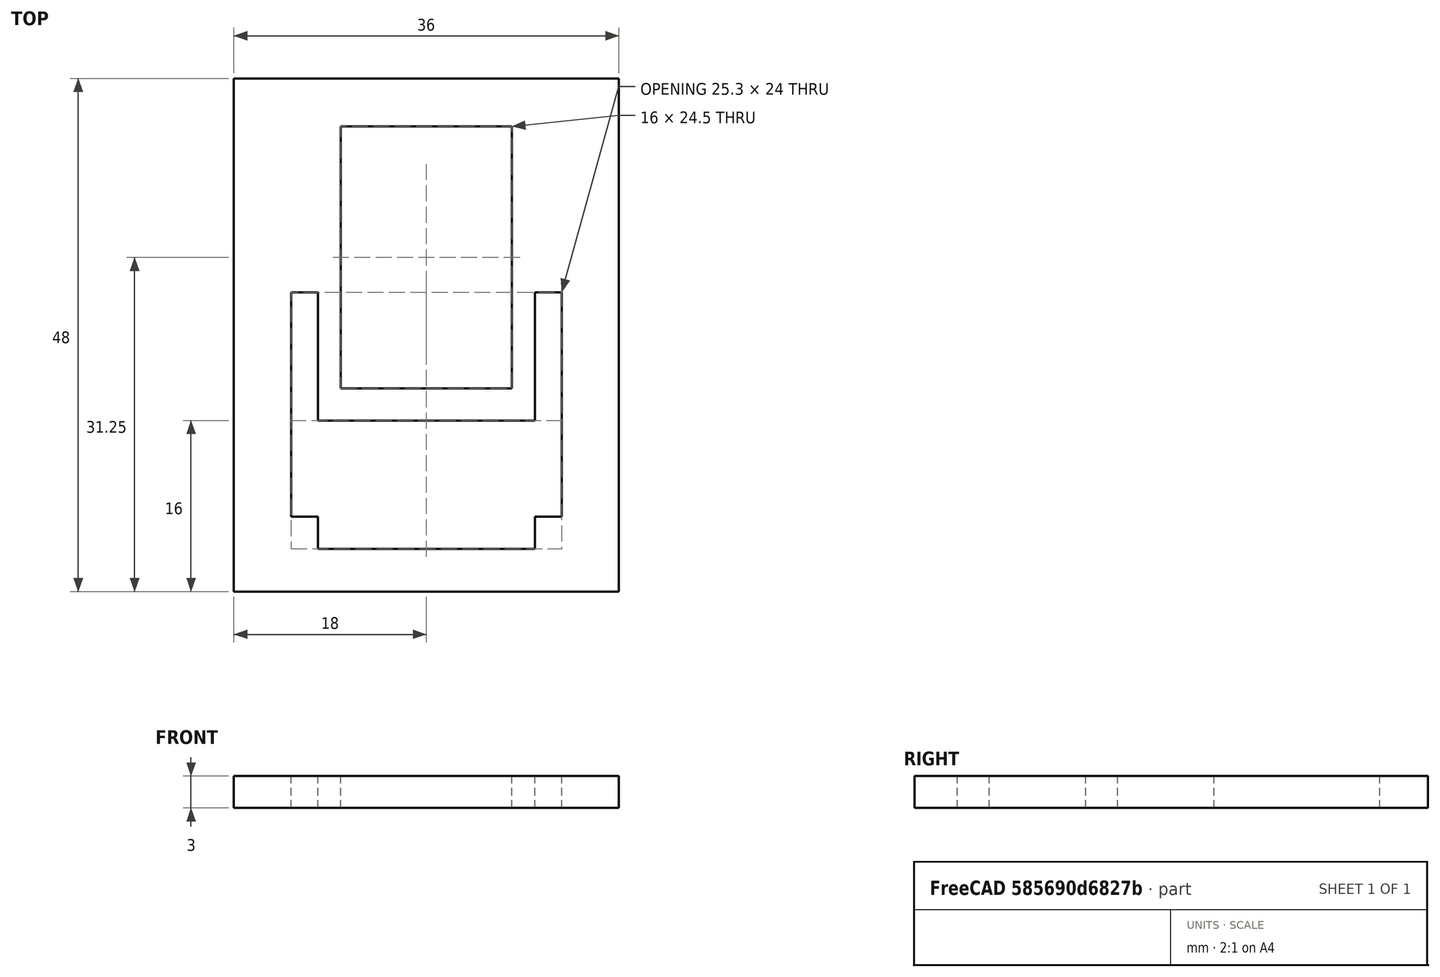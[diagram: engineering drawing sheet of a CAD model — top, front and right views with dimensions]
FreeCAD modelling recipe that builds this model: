
FCSTD DOCUMENT  (FreeCAD 0.20R29177 +426 (Git))
Label: ESP32CamCutOut
License: All rights reserved
LicenseURL: http://en.wikipedia.org/wiki/All_rights_reserved
objects: Sketcher::SketchObject×1, PartDesign::Pad×1, PartDesign::Body×1
note: 4 computed .brp shape members not serialized (recipe doc carries the construction recipe); baked Part::Feature solids carry a one-line shape summary decoded from their .brp

FEATURE [Sketcher::SketchObject] Sketch
  FullyConstrained = true
  MapMode = 5
  Support = -> [XY_Plane]
  sketch-geometry (20):
    g0: LineSegment StartX=-18 StartY=24 StartZ=0 EndX=18 EndY=24 EndZ=0
    g1: LineSegment StartX=18 StartY=24 StartZ=0 EndX=18 EndY=-24 EndZ=0
    g2: LineSegment StartX=18 StartY=-24 StartZ=0 EndX=-18 EndY=-24 EndZ=0
    g3: LineSegment StartX=-18 StartY=-24 StartZ=0 EndX=-18 EndY=24 EndZ=0
    g4: LineSegment StartX=-12.65 StartY=4 StartZ=0 EndX=-10.15 EndY=4 EndZ=0
    g5: LineSegment StartX=-12.65 StartY=4 StartZ=0 EndX=-12.65 EndY=-17 EndZ=0
    g6: LineSegment StartX=-12.65 StartY=-17 StartZ=0 EndX=-10.15 EndY=-17 EndZ=0
    g7: LineSegment StartX=-10.15 StartY=-17 StartZ=0 EndX=-10.15 EndY=-20 EndZ=0
    g8: LineSegment StartX=-10.15 StartY=-20 StartZ=0 EndX=10.15 EndY=-20 EndZ=0
    g9: LineSegment StartX=10.15 StartY=-20 StartZ=0 EndX=10.15 EndY=-17 EndZ=0
    g10: LineSegment StartX=10.15 StartY=-17 StartZ=0 EndX=12.65 EndY=-17 EndZ=0
    g11: LineSegment StartX=12.65 StartY=-17 StartZ=0 EndX=12.65 EndY=4 EndZ=0
    g12: LineSegment StartX=12.65 StartY=4 StartZ=0 EndX=10.15 EndY=4 EndZ=0
    g13: LineSegment StartX=10.15 StartY=4 StartZ=0 EndX=10.15 EndY=-8 EndZ=0
    g14: LineSegment StartX=10.15 StartY=-8 StartZ=0 EndX=-10.15 EndY=-8 EndZ=0
    g15: LineSegment StartX=-10.15 StartY=-8 StartZ=0 EndX=-10.15 EndY=4 EndZ=0
    g16: LineSegment StartX=-8 StartY=19.5 StartZ=0 EndX=8 EndY=19.5 EndZ=0
    g17: LineSegment StartX=8 StartY=19.5 StartZ=0 EndX=8 EndY=-5 EndZ=0
    g18: LineSegment StartX=8 StartY=-5 StartZ=0 EndX=-8 EndY=-5 EndZ=0
    g19: LineSegment StartX=-8 StartY=-5 StartZ=0 EndX=-8 EndY=19.5 EndZ=0
  constraints (56):
    c: Coincident(g0,g1)
    c: Coincident(g1,g2)
    c: Coincident(g2,g3)
    c: Coincident(g3,g0)
    c: Horizontal(g2)
    c: Vertical(g3)
    c: DistanceX(g0,g0) = 36
    c: DistanceY(g1,g0) = 48
    c: Symmetric(g0,g0,g-2)
    c: Symmetric(g0,g1,g-1)
    c: Horizontal(g4)
    c: Coincident(g4,g5)
    c: Vertical(g5)
    c: Coincident(g5,g6)
    c: Horizontal(g6)
    c: Coincident(g6,g7)
    c: Vertical(g7)
    c: Coincident(g7,g8)
    c: Horizontal(g8)
    c: Coincident(g8,g9)
    c: Vertical(g9)
    c: Coincident(g9,g10)
    c: Horizontal(g10)
    c: Coincident(g10,g11)
    c: Vertical(g11)
    c: Coincident(g11,g12)
    c: Horizontal(g12)
    c: Coincident(g12,g13)
    c: Coincident(g13,g14)
    c: Coincident(g14,g15)
    c: Coincident(g15,g4)
    c: Vertical(g15)
    c: Vertical(g13)
    c: DistanceX(g4,g4) = 2.5
    c: Equal(g4,g6)
    c: Equal(g4,g12)
    c: Equal(g4,g10)
    c: DistanceX(g14,g14) = 20.3
    c: Symmetric(g14,g13,g-2)
    c: Horizontal(g4,g12)
    c: DistanceY(g2,g7) = 4
    c: DistanceY(g5,g5) = 21
    c: DistanceY(g7,g7) = 3
    c: DistanceY(g7,g14) = 12
    c: Horizontal(g9,g6)
    c: Coincident(g16,g17)
    c: Coincident(g17,g18)
    c: Coincident(g18,g19)
    c: Coincident(g19,g16)
    c: Horizontal(g16)
    c: Vertical(g17)
    c: Vertical(g19)
    c: DistanceY(g8,g17) = 15
    c: DistanceY(g17,g16) = 24.5
    c: Symmetric(g17,g18,g-2)
    c: DistanceX(g16,g16) = 16
FEATURE [PartDesign::Pad] Pad
  Direction = (0,0,1)
  Length = 3
  Length2 = 10
  Profile = -> Sketch
  ReferenceAxis = -> Sketch [N_Axis]
  Type = 0
FEATURE [PartDesign::Body] Body
  Group = -> [Sketch,Pad]
  Origin = -> Origin
  Tip = -> Pad
